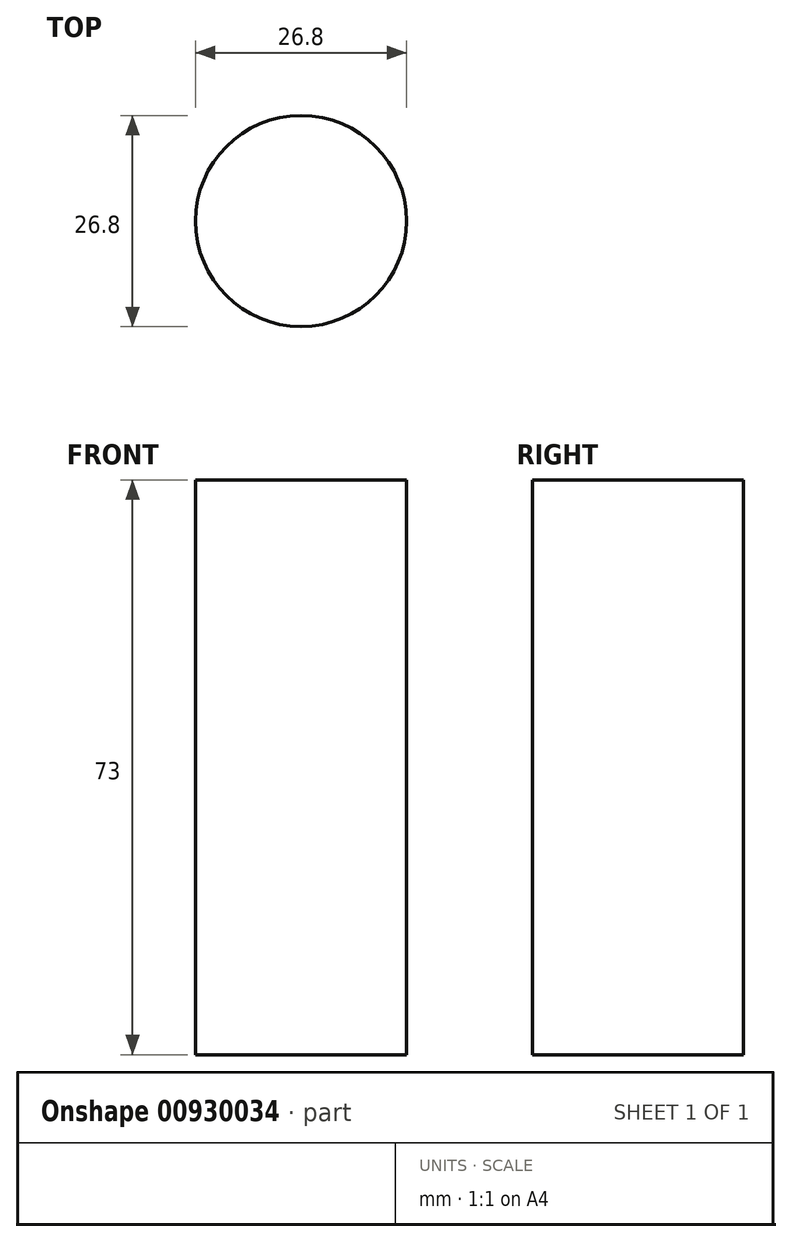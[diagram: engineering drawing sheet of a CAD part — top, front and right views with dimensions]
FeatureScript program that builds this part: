
annotation { "Feature Type Name" : "Feature", "Feature Type Description" : "" }
export const myFeature = defineFeature(function(context is Context, id is Id, definition is map)
    precondition{}
    {
        {
            var Q0;
            Q0=qCreatedBy(makeId("Top.planeOp"),FACE);
            var sketch = newSketch(context, id + "F0", { "sketchPlane" : qUnion([Q0])});
            skCircle(sketch, "E0", {"center": v(-0.07, -0.07) * mm, "radius": 5.12 * mm});
            skCircle(sketch, "E1", {"center": v(-0.07, -0.07) * mm, "radius": 22.1 * mm});
            skCircle(sketch, "E2", {"center": v(-0.07, -0.07) * mm, "radius": 5.14 * mm});
            skCircle(sketch, "E3", {"center": v(0, -22.17) * mm, "radius": 11.9 * mm, "construction": true});
            skCircle(sketch, "E4", {"center": v(22.03, 0) * mm, "radius": 10.62 * mm, "construction": true});
            skCircle(sketch, "E5", {"center": v(0, 22.03) * mm, "radius": 9.43 * mm, "construction": true});
            skCircle(sketch, "E6", {"center": v(-22.17, 0) * mm, "radius": 8.79 * mm, "construction": true});
            skCircle(sketch, "E7", {"center": v(0, -22.17) * mm, "radius": 12.9 * mm});
            skCircle(sketch, "E8", {"center": v(22.03, 0) * mm, "radius": 11.62 * mm});
            skCircle(sketch, "E9", {"center": v(0, 22.03) * mm, "radius": 10.43 * mm});
            skCircle(sketch, "E10", {"center": v(-22.17, 0) * mm, "radius": 9.8 * mm});
            skCircle(sketch, "E11", {"center": v(-22.17, 0) * mm, "radius": 10.3 * mm});
            skCircle(sketch, "E12", {"center": v(0, -22.17) * mm, "radius": 13.4 * mm});
            skCircle(sketch, "E13", {"center": v(22.03, 0) * mm, "radius": 12.12 * mm});
            skCircle(sketch, "E14", {"center": v(0, 22.03) * mm, "radius": 10.93 * mm});
            skSolve(sketch);
        }
        {
            var Q0;
            {var subQ0=sQuery(id+"F0.wireOp",EDGE,"E12");var subQ1=sQuery(id+"F0.wireOp",EDGE,"E1");var subQ2=makeQuery(id+"F0.imprint","INTERSECT",VERTEX,{"disambiguationData":[OD(0.0)],"derivedFrom":[subQ1,subQ0]});Q0=makeQuery(id+"F0.imprint","IMPRINT",FACE,{"disambiguationData":[TD([[makeQuery(id+"F0.imprint","IMPRINT",EDGE,{"disambiguationData":[TD([[subQ2,-1.0]])],"derivedFrom":subQ1}),-1.0]])]});}
            var Q1;
            {var subQ0=sQuery(id+"F0.wireOp",EDGE,"E12");var subQ1=sQuery(id+"F0.wireOp",EDGE,"E1");var subQ2=makeQuery(id+"F0.imprint","INTERSECT",VERTEX,{"disambiguationData":[OD(0.0)],"derivedFrom":[subQ1,subQ0]});Q1=makeQuery(id+"F0.imprint","IMPRINT",FACE,{"disambiguationData":[TD([[makeQuery(id+"F0.imprint","IMPRINT",EDGE,{"disambiguationData":[TD([[subQ2,-1.0]])],"derivedFrom":subQ1}),1.0]])]});}
            var Q2;
            {var subQ0=sQuery(id+"F0.wireOp",EDGE,"E7");var subQ1=sQuery(id+"F0.wireOp",EDGE,"E1");var subQ2=makeQuery(id+"F0.imprint","INTERSECT",VERTEX,{"disambiguationData":[OD(0.0)],"derivedFrom":[subQ1,subQ0]});Q2=makeQuery(id+"F0.imprint","IMPRINT",FACE,{"disambiguationData":[TD([[makeQuery(id+"F0.imprint","IMPRINT",EDGE,{"disambiguationData":[TD([[subQ2,-1.0]])],"derivedFrom":subQ1}),-1.0]])]});}
            var Q3;
            {var subQ0=sQuery(id+"F0.wireOp",EDGE,"E7");var subQ1=sQuery(id+"F0.wireOp",EDGE,"E1");var subQ2=makeQuery(id+"F0.imprint","INTERSECT",VERTEX,{"disambiguationData":[OD(0.0)],"derivedFrom":[subQ1,subQ0]});Q3=makeQuery(id+"F0.imprint","IMPRINT",FACE,{"disambiguationData":[TD([[makeQuery(id+"F0.imprint","IMPRINT",EDGE,{"disambiguationData":[TD([[subQ2,-1.0]])],"derivedFrom":subQ1}),1.0]])]});}
            extrude(context, id + "F1", {"entities" : qUnion([Q0, Q1, Q2, Q3]), "depth" : 73 * mm, "offsetDistance" : 25 * mm});
        }
    });
